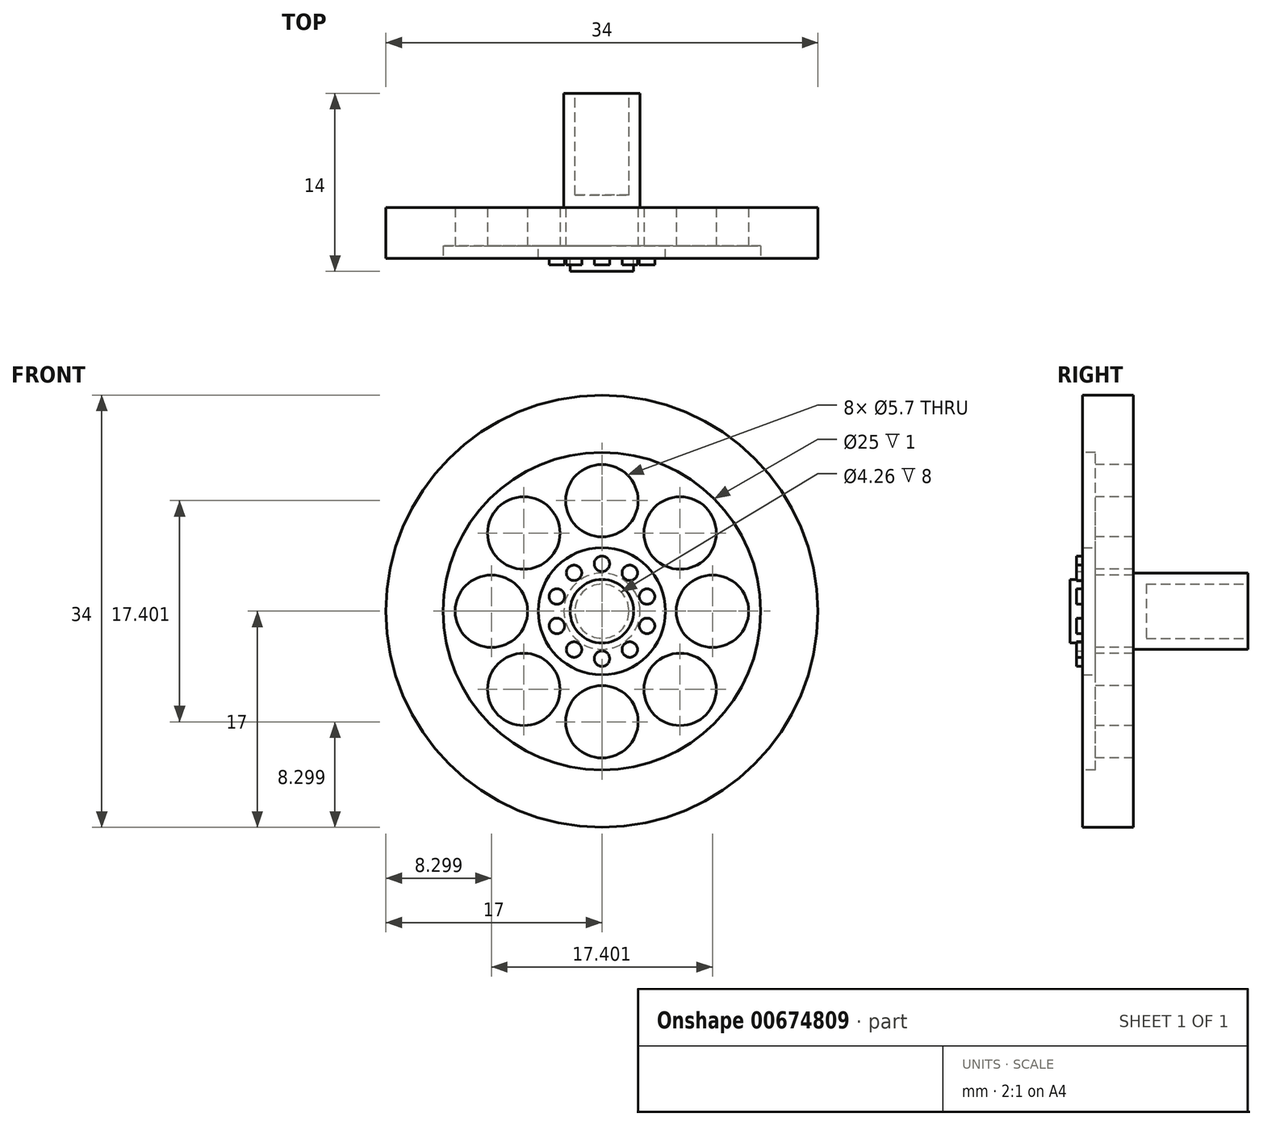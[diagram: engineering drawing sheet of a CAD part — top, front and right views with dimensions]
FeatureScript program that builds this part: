
annotation { "Feature Type Name" : "Feature", "Feature Type Description" : "" }
export const myFeature = defineFeature(function(context is Context, id is Id, definition is map)
    precondition{}
    {
        {
            var Q0;
            Q0=qCreatedBy(makeId("Front.planeOp"),FACE);
            var sketch = newSketch(context, id + "F0", { "sketchPlane" : qUnion([Q0])});
            skCircle(sketch, "E0", {"center": v(0, 0) * mm, "radius": 17 * mm});
            skSolve(sketch);
        }
        {
            var Q0;
            Q0=makeQuery(id+"F0.imprint","IMPRINT",FACE,{"disambiguationData":[TD([[makeQuery(id+"F0.imprint","IMPRINT",EDGE,{"derivedFrom":sQuery(id+"F0.wireOp",EDGE,"E0")}),1.0]])]});
            extrude(context, id + "F1", {"entities" : qUnion([Q0]), "depth" : 4 * mm, "offsetDistance" : 25.4 * mm});
        }
        {
            var Q0;
            Q0=makeQuery(id+"F1.opExtrude","CAP_FACE",FACE,{"disambiguationData":[OSD([sQuery(id+"F0.wireOp",EDGE,"E0")])],"isStart":false});
            var sketch = newSketch(context, id + "F2", { "sketchPlane" : qUnion([Q0])});
            skCircle(sketch, "E1", {"center": v(0, 0) * mm, "radius": 12.5 * mm});
            skSolve(sketch);
        }
        {
            var Q0;
            Q0=makeQuery(id+"F2.imprint","IMPRINT",FACE,{"disambiguationData":[TD([[makeQuery(id+"F2.imprint","IMPRINT",EDGE,{"derivedFrom":sQuery(id+"F2.wireOp",EDGE,"E1")}),1.0]])]});
            extrude(context, id + "F3", {"entities" : qUnion([Q0]), "operationType" : NewBodyOperationType.REMOVE, "oppositeDirection" : true, "depth" : 1 * mm, "offsetDistance" : 25.4 * mm});
        }
        {
            var Q0;
            Q0=makeQuery(id+"F3.boolean.opBoolean","COPY",FACE,{"derivedFrom":makeQuery(id+"F3.opExtrude","CAP_FACE",FACE,{"disambiguationData":[OSD([sQuery(id+"F2.wireOp",EDGE,"E1")])],"isStart":false})});
            var sketch = newSketch(context, id + "F4", { "sketchPlane" : qUnion([Q0])});
            skCircle(sketch, "E2", {"center": v(0, 0) * mm, "radius": 5 * mm});
            skSolve(sketch);
        }
        {
            var Q0;
            Q0=makeQuery(id+"F4.imprint","IMPRINT",FACE,{"disambiguationData":[TD([[makeQuery(id+"F4.imprint","IMPRINT",EDGE,{"derivedFrom":sQuery(id+"F4.wireOp",EDGE,"E2")}),1.0]])]});
            extrude(context, id + "F5", {"entities" : qUnion([Q0]), "operationType" : NewBodyOperationType.ADD, "depth" : 1 * mm, "offsetDistance" : 25.4 * mm});
        }
        {
            var Q0;
            Q0=makeQuery(id+"F5.opExtrude","CAP_FACE",FACE,{"disambiguationData":[OSD([sQuery(id+"F4.wireOp",EDGE,"E2")])],"isStart":false});
            var sketch = newSketch(context, id + "F6", { "sketchPlane" : qUnion([Q0])});
            skCircle(sketch, "E3", {"center": v(0, 0) * mm, "radius": 2.5 * mm});
            skSolve(sketch);
        }
        {
            var Q0;
            Q0=makeQuery(id+"F6.imprint","IMPRINT",FACE,{"disambiguationData":[TD([[makeQuery(id+"F6.imprint","IMPRINT",EDGE,{"derivedFrom":sQuery(id+"F6.wireOp",EDGE,"E3")}),1.0]])]});
            extrude(context, id + "F7", {"entities" : qUnion([Q0]), "operationType" : NewBodyOperationType.ADD, "depth" : 1 * mm, "offsetDistance" : 25.4 * mm});
        }
        {
            var Q0;
            Q0=makeQuery(id+"F3.boolean.opBoolean","COPY",FACE,{"derivedFrom":makeQuery(id+"F3.opExtrude","CAP_FACE",FACE,{"disambiguationData":[OSD([sQuery(id+"F2.wireOp",EDGE,"E1")])],"isStart":false})});
            var sketch = newSketch(context, id + "F8", { "sketchPlane" : qUnion([Q0])});
            skCircle(sketch, "E4", {"center": v(0, 8.7) * mm, "radius": 2.85 * mm});
            skCircle(sketch, "E5.1.0", {"center": v(-6.15, 6.15) * mm, "radius": 2.85 * mm});
            skCircle(sketch, "E5.2.0", {"center": v(-8.7, 0) * mm, "radius": 2.85 * mm});
            skCircle(sketch, "E5.3.0", {"center": v(-6.15, -6.15) * mm, "radius": 2.85 * mm});
            skCircle(sketch, "E5.4.0", {"center": v(0, -8.7) * mm, "radius": 2.85 * mm});
            skCircle(sketch, "E5.5.0", {"center": v(6.15, -6.15) * mm, "radius": 2.85 * mm});
            skCircle(sketch, "E5.6.0", {"center": v(8.7, 0) * mm, "radius": 2.85 * mm});
            skCircle(sketch, "E5.7.0", {"center": v(6.15, 6.15) * mm, "radius": 2.85 * mm});
            skPoint(sketch, "E5.center", {"position": v(0, 0) * mm});
            skSolve(sketch);
        }
        {
            var Q0;
            Q0=makeQuery(id+"F8.imprint","IMPRINT",FACE,{"disambiguationData":[TD([[makeQuery(id+"F8.imprint","IMPRINT",EDGE,{"derivedFrom":sQuery(id+"F8.wireOp",EDGE,"E5.1.0")}),1.0]])]});
            var Q1;
            Q1=makeQuery(id+"F8.imprint","IMPRINT",FACE,{"disambiguationData":[TD([[makeQuery(id+"F8.imprint","IMPRINT",EDGE,{"derivedFrom":sQuery(id+"F8.wireOp",EDGE,"E5.2.0")}),1.0]])]});
            var Q2;
            Q2=makeQuery(id+"F8.imprint","IMPRINT",FACE,{"disambiguationData":[TD([[makeQuery(id+"F8.imprint","IMPRINT",EDGE,{"derivedFrom":sQuery(id+"F8.wireOp",EDGE,"E5.3.0")}),1.0]])]});
            var Q3;
            Q3=makeQuery(id+"F8.imprint","IMPRINT",FACE,{"disambiguationData":[TD([[makeQuery(id+"F8.imprint","IMPRINT",EDGE,{"derivedFrom":sQuery(id+"F8.wireOp",EDGE,"E5.4.0")}),1.0]])]});
            var Q4;
            Q4=makeQuery(id+"F8.imprint","IMPRINT",FACE,{"disambiguationData":[TD([[makeQuery(id+"F8.imprint","IMPRINT",EDGE,{"derivedFrom":sQuery(id+"F8.wireOp",EDGE,"E5.5.0")}),1.0]])]});
            var Q5;
            Q5=makeQuery(id+"F8.imprint","IMPRINT",FACE,{"disambiguationData":[TD([[makeQuery(id+"F8.imprint","IMPRINT",EDGE,{"derivedFrom":sQuery(id+"F8.wireOp",EDGE,"E5.6.0")}),1.0]])]});
            var Q6;
            Q6=makeQuery(id+"F8.imprint","IMPRINT",FACE,{"disambiguationData":[TD([[makeQuery(id+"F8.imprint","IMPRINT",EDGE,{"derivedFrom":sQuery(id+"F8.wireOp",EDGE,"E5.7.0")}),1.0]])]});
            var Q7;
            Q7=makeQuery(id+"F8.imprint","IMPRINT",FACE,{"disambiguationData":[TD([[makeQuery(id+"F8.imprint","IMPRINT",EDGE,{"derivedFrom":sQuery(id+"F8.wireOp",EDGE,"E4")}),1.0]])]});
            extrude(context, id + "F9", {"entities" : qUnion([Q0, Q1, Q2, Q3, Q4, Q5, Q6, Q7]), "operationType" : NewBodyOperationType.REMOVE, "oppositeDirection" : true, "depth" : 5 * mm, "offsetDistance" : 25.4 * mm});
        }
        {
            var Q0;
            Q0=makeQuery(id+"F5.opExtrude","CAP_FACE",FACE,{"disambiguationData":[OSD([sQuery(id+"F4.wireOp",EDGE,"E2")])],"isStart":false});
            var sketch = newSketch(context, id + "F10", { "sketchPlane" : qUnion([Q0])});
            skCircle(sketch, "E6", {"center": v(0, 3.73) * mm, "radius": 0.6 * mm});
            skCircle(sketch, "E7.1.0", {"center": v(-2.2, 3.02) * mm, "radius": 0.6 * mm});
            skCircle(sketch, "E7.2.0", {"center": v(-3.55, 1.15) * mm, "radius": 0.6 * mm});
            skCircle(sketch, "E7.3.0", {"center": v(-3.55, -1.15) * mm, "radius": 0.6 * mm});
            skCircle(sketch, "E7.4.0", {"center": v(-2.2, -3.02) * mm, "radius": 0.6 * mm});
            skCircle(sketch, "E7.5.0", {"center": v(0, -3.73) * mm, "radius": 0.6 * mm});
            skCircle(sketch, "E7.6.0", {"center": v(2.2, -3.02) * mm, "radius": 0.6 * mm});
            skCircle(sketch, "E7.7.0", {"center": v(3.55, -1.15) * mm, "radius": 0.6 * mm});
            skCircle(sketch, "E7.8.0", {"center": v(3.55, 1.15) * mm, "radius": 0.6 * mm});
            skCircle(sketch, "E7.9.0", {"center": v(2.2, 3.02) * mm, "radius": 0.6 * mm});
            skPoint(sketch, "E7.center", {"position": v(0, 0) * mm});
            skSolve(sketch);
        }
        {
            var Q0;
            Q0=makeQuery(id+"F10.imprint","IMPRINT",FACE,{"disambiguationData":[TD([[makeQuery(id+"F10.imprint","IMPRINT",EDGE,{"derivedFrom":sQuery(id+"F10.wireOp",EDGE,"E6")}),1.0]])]});
            var Q1;
            Q1=makeQuery(id+"F10.imprint","IMPRINT",FACE,{"disambiguationData":[TD([[makeQuery(id+"F10.imprint","IMPRINT",EDGE,{"derivedFrom":sQuery(id+"F10.wireOp",EDGE,"E7.1.0")}),1.0]])]});
            var Q2;
            Q2=makeQuery(id+"F10.imprint","IMPRINT",FACE,{"disambiguationData":[TD([[makeQuery(id+"F10.imprint","IMPRINT",EDGE,{"derivedFrom":sQuery(id+"F10.wireOp",EDGE,"E7.2.0")}),1.0]])]});
            var Q3;
            Q3=makeQuery(id+"F10.imprint","IMPRINT",FACE,{"disambiguationData":[TD([[makeQuery(id+"F10.imprint","IMPRINT",EDGE,{"derivedFrom":sQuery(id+"F10.wireOp",EDGE,"E7.3.0")}),1.0]])]});
            var Q4;
            Q4=makeQuery(id+"F10.imprint","IMPRINT",FACE,{"disambiguationData":[TD([[makeQuery(id+"F10.imprint","IMPRINT",EDGE,{"derivedFrom":sQuery(id+"F10.wireOp",EDGE,"E7.4.0")}),1.0]])]});
            var Q5;
            Q5=makeQuery(id+"F10.imprint","IMPRINT",FACE,{"disambiguationData":[TD([[makeQuery(id+"F10.imprint","IMPRINT",EDGE,{"derivedFrom":sQuery(id+"F10.wireOp",EDGE,"E7.5.0")}),1.0]])]});
            var Q6;
            Q6=makeQuery(id+"F10.imprint","IMPRINT",FACE,{"disambiguationData":[TD([[makeQuery(id+"F10.imprint","IMPRINT",EDGE,{"derivedFrom":sQuery(id+"F10.wireOp",EDGE,"E7.6.0")}),1.0]])]});
            var Q7;
            Q7=makeQuery(id+"F10.imprint","IMPRINT",FACE,{"disambiguationData":[TD([[makeQuery(id+"F10.imprint","IMPRINT",EDGE,{"derivedFrom":sQuery(id+"F10.wireOp",EDGE,"E7.7.0")}),1.0]])]});
            var Q8;
            Q8=makeQuery(id+"F10.imprint","IMPRINT",FACE,{"disambiguationData":[TD([[makeQuery(id+"F10.imprint","IMPRINT",EDGE,{"derivedFrom":sQuery(id+"F10.wireOp",EDGE,"E7.8.0")}),1.0]])]});
            var Q9;
            Q9=makeQuery(id+"F10.imprint","IMPRINT",FACE,{"disambiguationData":[TD([[makeQuery(id+"F10.imprint","IMPRINT",EDGE,{"derivedFrom":sQuery(id+"F10.wireOp",EDGE,"E7.9.0")}),1.0]])]});
            extrude(context, id + "F11", {"entities" : qUnion([Q0, Q1, Q2, Q3, Q4, Q5, Q6, Q7, Q8, Q9]), "operationType" : NewBodyOperationType.ADD, "depth" : .5 * mm, "offsetDistance" : 25.4 * mm});
        }
        {
            var Q0;
            Q0=makeQuery(id+"F1.opExtrude","CAP_FACE",FACE,{"disambiguationData":[OSD([sQuery(id+"F0.wireOp",EDGE,"E0")])],"isStart":true});
            var sketch = newSketch(context, id + "F12", { "sketchPlane" : qUnion([Q0])});
            skCircle(sketch, "E8", {"center": v(0, 0) * mm, "radius": 3 * mm});
            skSolve(sketch);
        }
        {
            var Q0;
            Q0=makeQuery(id+"F12.imprint","IMPRINT",FACE,{"disambiguationData":[TD([[makeQuery(id+"F12.imprint","IMPRINT",EDGE,{"derivedFrom":sQuery(id+"F12.wireOp",EDGE,"E8")}),1.0]])]});
            extrude(context, id + "F13", {"entities" : qUnion([Q0]), "operationType" : NewBodyOperationType.ADD, "depth" : 9 * mm, "offsetDistance" : 25.4 * mm});
        }
        {
            var Q0;
            Q0=makeQuery(id+"F13.opExtrude","CAP_FACE",FACE,{"disambiguationData":[OSD([sQuery(id+"F12.wireOp",EDGE,"E8")])],"isStart":false});
            var sketch = newSketch(context, id + "F14", { "sketchPlane" : qUnion([Q0])});
            skCircle(sketch, "E9", {"center": v(0, 0) * mm, "radius": 2.13 * mm});
            skSolve(sketch);
        }
        {
            var Q0;
            Q0=makeQuery(id+"F14.imprint","IMPRINT",FACE,{"disambiguationData":[TD([[makeQuery(id+"F14.imprint","IMPRINT",EDGE,{"derivedFrom":sQuery(id+"F14.wireOp",EDGE,"E9")}),1.0]])]});
            extrude(context, id + "F15", {"entities" : qUnion([Q0]), "operationType" : NewBodyOperationType.REMOVE, "oppositeDirection" : true, "depth" : 8 * mm, "offsetDistance" : 25.4 * mm});
        }
    });
